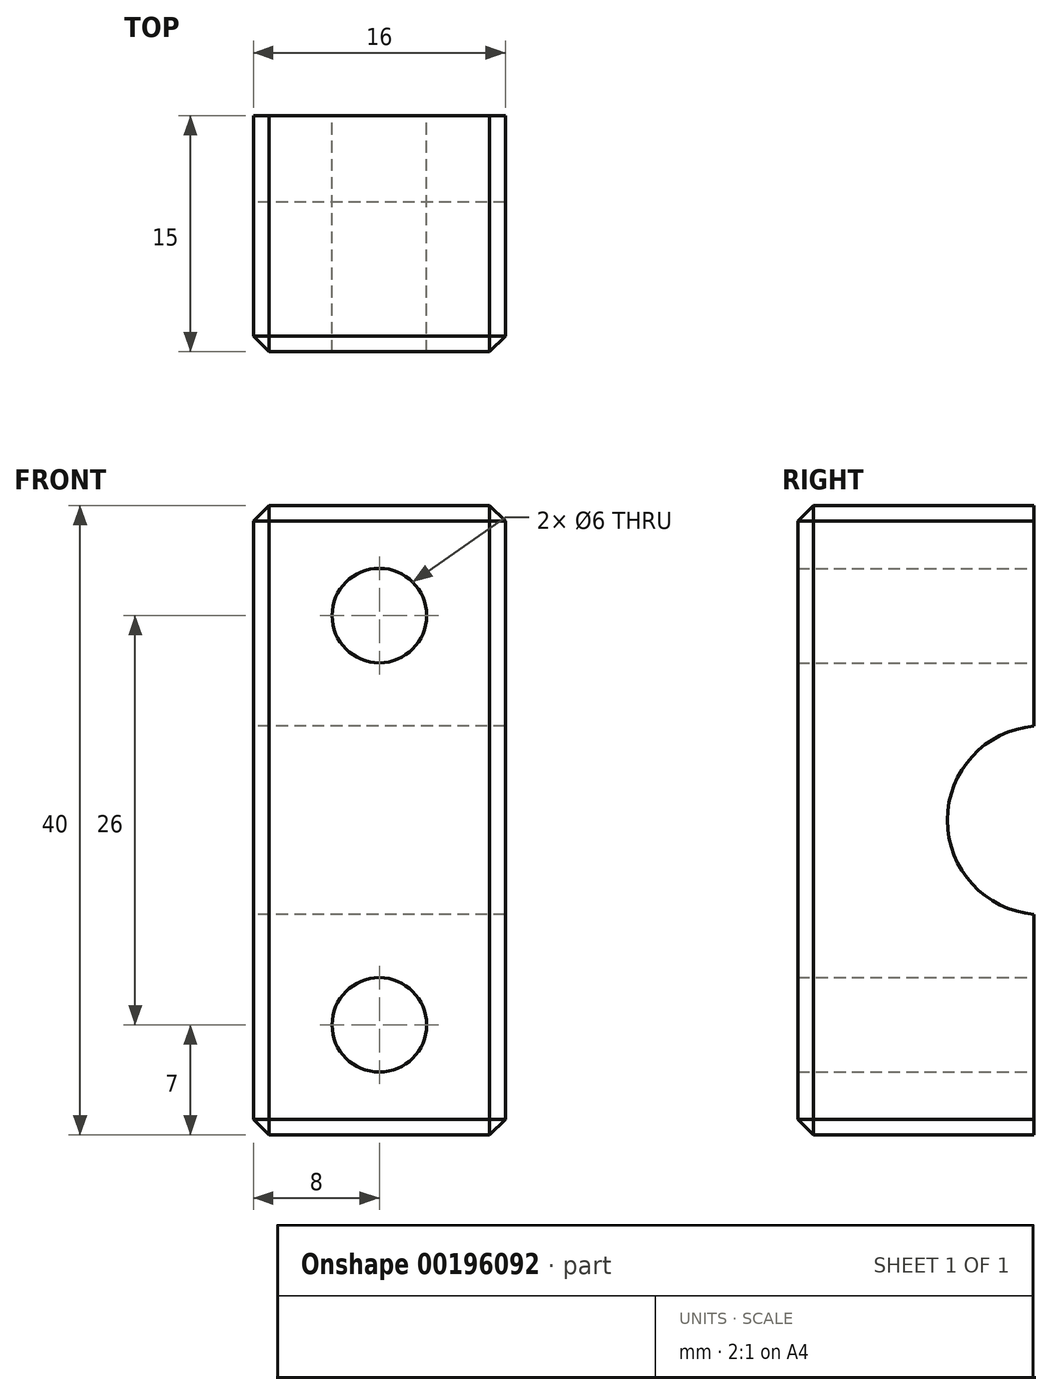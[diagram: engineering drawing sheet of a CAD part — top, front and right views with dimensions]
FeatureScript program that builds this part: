
annotation { "Feature Type Name" : "Feature", "Feature Type Description" : "" }
export const myFeature = defineFeature(function(context is Context, id is Id, definition is map)
    precondition{}
    {
        {
            var Q0;
            Q0=qCreatedBy(makeId("Front.planeOp"),FACE);
            var sketch = newSketch(context, id + "F0", { "sketchPlane" : qUnion([Q0])});
            skLineSegment(sketch, "E0.bottom", {"start": v(8, 20) * mm, "end": v(-8, 20) * mm});
            skLineSegment(sketch, "E0.top", {"start": v(8, -20) * mm, "end": v(-8, -20) * mm});
            skLineSegment(sketch, "E0.left", {"start": v(8, 20) * mm, "end": v(8, -20) * mm});
            skLineSegment(sketch, "E0.right", {"start": v(-8, 20) * mm, "end": v(-8, -20) * mm});
            skPoint(sketch, "E0.middle", {"position": v(0, 0) * mm});
            skSolve(sketch);
        }
        {
            var Q0;
            Q0=makeQuery(id+"F0.imprint","IMPRINT",FACE,{"disambiguationData":[TD([[makeQuery(id+"F0.imprint","IMPRINT",EDGE,{"derivedFrom":sQuery(id+"F0.wireOp",EDGE,"E0.bottom")}),1.0]])]});
            extrude(context, id + "F1", {"entities" : qUnion([Q0]), "depth" : 15 * mm});
        }
        {
            var Q0;
            Q0=makeQuery(id+"F1.opExtrude","SWEPT_FACE",FACE,{"disambiguationData":[OSD([sQuery(id+"F0.wireOp",EDGE,"E0.right")])]});
            var sketch = newSketch(context, id + "F2", { "sketchPlane" : qUnion([Q0])});
            skCircle(sketch, "E1", {"center": v(-0.5, 0) * mm, "radius": 6 * mm});
            skSolve(sketch);
        }
        {
            var Q0;
            Q0 = qSketchRegion(id + "F2", true);
            extrude(context, id + "F3", {"entities" : qUnion([Q0]), "operationType" : NewBodyOperationType.REMOVE, "endBound" : BoundingType.THROUGH_ALL, "oppositeDirection" : true, "depth" : 25 * mm});
        }
        {
            var Q0;
            Q0=qCreatedBy(makeId("Front.planeOp"),FACE);
            var sketch = newSketch(context, id + "F4", { "sketchPlane" : qUnion([Q0])});
            skCircle(sketch, "E2", {"center": v(0, 13) * mm, "radius": 3 * mm});
            skCircle(sketch, "E3.MirrorC", {"center": v(0, -13) * mm, "radius": 3 * mm});
            skSolve(sketch);
        }
        {
            var Q0;
            Q0 = qSketchRegion(id + "F4", true);
            extrude(context, id + "F5", {"entities" : qUnion([Q0]), "operationType" : NewBodyOperationType.REMOVE, "endBound" : BoundingType.THROUGH_ALL, "depth" : 25 * mm});
        }
        {
            var Q0;
            Q0=makeQuery(id+"F1.opExtrude","SWEPT_EDGE",EDGE,{"disambiguationData":[OSD([sQuery(id+"F0.wireOp",EDGE,"E0.bottom"),sQuery(id+"F0.wireOp",EDGE,"E0.left")])]});
            var Q1;
            Q1=makeQuery(id+"F1.opExtrude","SWEPT_EDGE",EDGE,{"disambiguationData":[OSD([sQuery(id+"F0.wireOp",EDGE,"E0.bottom"),sQuery(id+"F0.wireOp",EDGE,"E0.right")])]});
            var Q2;
            Q2=makeQuery(id+"F1.opExtrude","SWEPT_EDGE",EDGE,{"disambiguationData":[OSD([sQuery(id+"F0.wireOp",EDGE,"E0.top"),sQuery(id+"F0.wireOp",EDGE,"E0.left")])]});
            var Q3;
            Q3=makeQuery(id+"F1.opExtrude","SWEPT_EDGE",EDGE,{"disambiguationData":[OSD([sQuery(id+"F0.wireOp",EDGE,"E0.top"),sQuery(id+"F0.wireOp",EDGE,"E0.right")])]});
            var Q4;
            Q4=makeQuery(id+"F1.opExtrude","CAP_EDGE",EDGE,{"disambiguationData":[OSD([sQuery(id+"F0.wireOp",EDGE,"E0.right")])],"isStart":false});
            var Q5;
            Q5=makeQuery(id+"F1.opExtrude","CAP_EDGE",EDGE,{"disambiguationData":[OSD([sQuery(id+"F0.wireOp",EDGE,"E0.top")])],"isStart":false});
            var Q6;
            Q6=makeQuery(id+"F1.opExtrude","CAP_EDGE",EDGE,{"disambiguationData":[OSD([sQuery(id+"F0.wireOp",EDGE,"E0.left")])],"isStart":false});
            var Q7;
            Q7=makeQuery(id+"F1.opExtrude","CAP_EDGE",EDGE,{"disambiguationData":[OSD([sQuery(id+"F0.wireOp",EDGE,"E0.bottom")])],"isStart":false});
            chamfer(context, id + "F6", {"entities" : qUnion([Q0, Q1, Q2, Q3, Q4, Q5, Q6, Q7]), "width" : 1 * mm, "tangentPropagation" : true});
        }
    });
